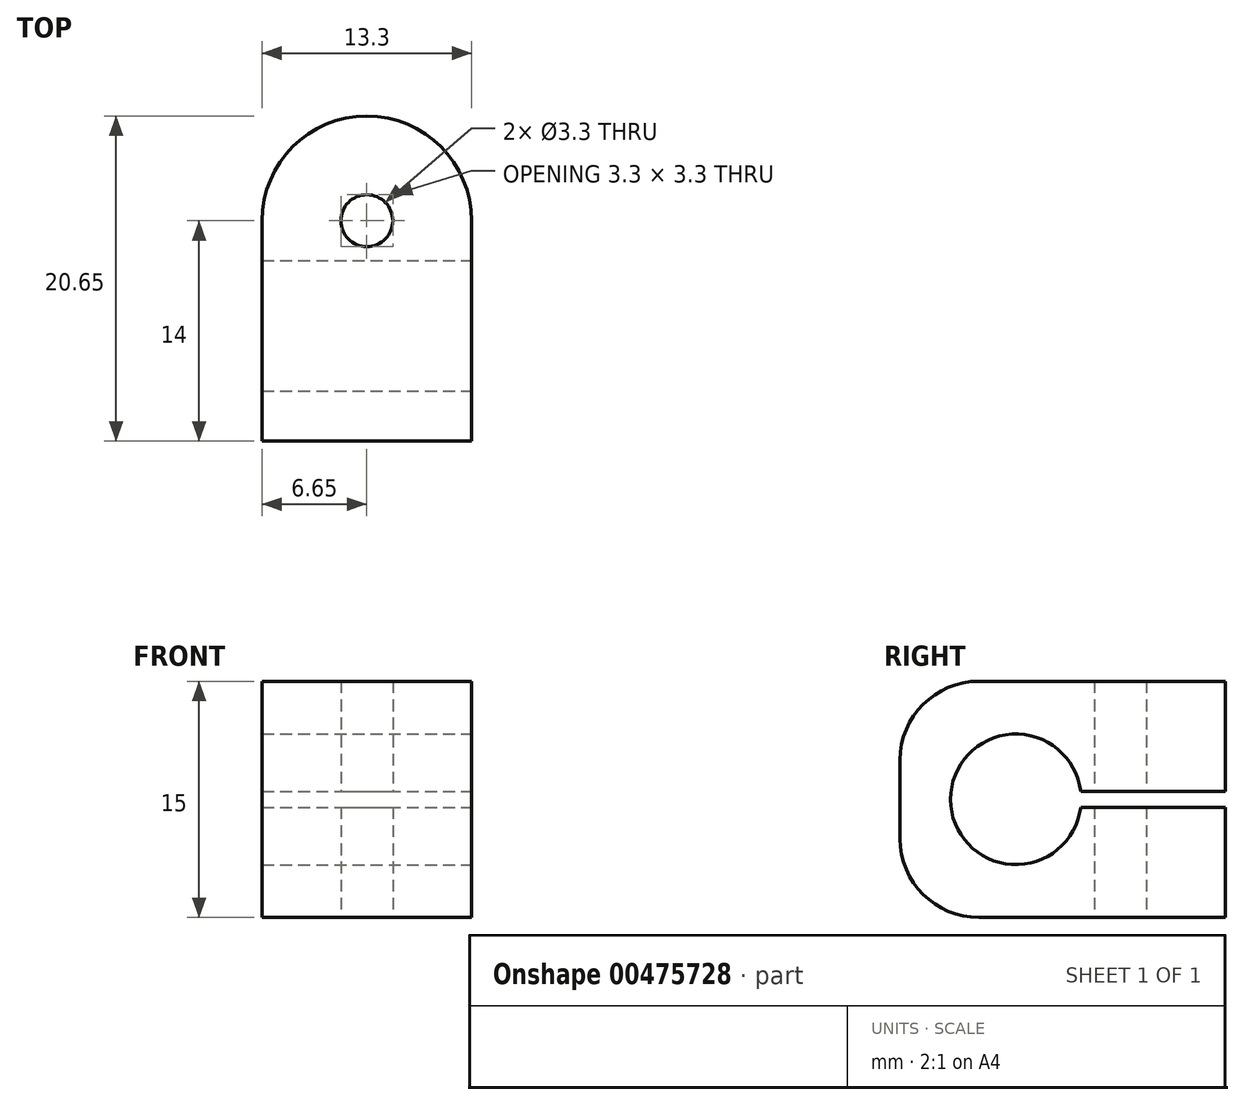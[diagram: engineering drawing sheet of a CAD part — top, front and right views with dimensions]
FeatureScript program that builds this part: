
annotation { "Feature Type Name" : "Feature", "Feature Type Description" : "" }
export const myFeature = defineFeature(function(context is Context, id is Id, definition is map)
    precondition{}
    {
        {
            var Q0;
            Q0=qCreatedBy(makeId("Top.planeOp"),FACE);
            var sketch = newSketch(context, id + "F0", { "sketchPlane" : qUnion([Q0])});
            skCircle(sketch, "E0", {"center": v(0, 0) * mm, "radius": 1.65 * mm});
            skCircle(sketch, "E1", {"center": v(0, 0) * mm, "radius": 6.65 * mm});
            skLineSegment(sketch, "E2.bottom", {"start": v(-6.65, 0) * mm, "end": v(6.65, 0) * mm});
            skLineSegment(sketch, "E2.top", {"start": v(-6.65, -14) * mm, "end": v(6.65, -14) * mm});
            skLineSegment(sketch, "E2.left", {"start": v(-6.65, 0) * mm, "end": v(-6.65, -14) * mm});
            skLineSegment(sketch, "E2.right", {"start": v(6.65, 0) * mm, "end": v(6.65, -14) * mm});
            skSolve(sketch);
        }
        {
            var Q0;
            Q0=qSketchRegion(id+"F0",true);
            extrude(context, id + "F1", {"entities" : qUnion([Q0]), "depth" : 15 * mm});
        }
        {
            var Q0;
            Q0=makeQuery(id+"F1.opExtrude","SWEPT_FACE",FACE,{"disambiguationData":[OSD([sQuery(id+"F0.wireOp",EDGE,"E2.right")])]});
            var sketch = newSketch(context, id + "F2", { "sketchPlane" : qUnion([Q0])});
            skCircle(sketch, "E3", {"center": v(-6.65, 7.5) * mm, "radius": 4.15 * mm});
            skPoint(sketch, "E3.centerSnap0", {"position": v(-14, 7.5) * mm});
            skLineSegment(sketch, "E4.bottom", {"start": v(-2.53, 8) * mm, "end": v(7.86, 8) * mm});
            skLineSegment(sketch, "E4.top", {"start": v(-2.53, 7) * mm, "end": v(7.86, 7) * mm});
            skLineSegment(sketch, "E4.left", {"start": v(-2.53, 8) * mm, "end": v(-2.53, 7) * mm});
            skLineSegment(sketch, "E4.right", {"start": v(7.86, 8) * mm, "end": v(7.86, 7) * mm});
            skLineSegment(sketch, "E5", {"start": v(-1.65, 0) * mm, "end": v(-1.65, 15) * mm});
            skLineSegment(sketch, "E6", {"start": v(1.65, 15) * mm, "end": v(1.65, 0) * mm});
            skLineSegment(sketch, "E7", {"start": v(-14, 7.5) * mm, "end": v(-2.53, 7.5) * mm});
            skSolve(sketch);
        }
        {
            var Q0;
            Q0=qSketchRegion(id+"F2",true);
            extrude(context, id + "F3", {"entities" : qUnion([Q0]), "operationType" : NewBodyOperationType.REMOVE, "endBound" : BoundingType.THROUGH_ALL, "oppositeDirection" : true, "depth" : 25 * mm});
        }
        {
            var Q0;
            Q0=makeQuery(id+"F1.opExtrude","CAP_EDGE",EDGE,{"disambiguationData":[OSD([sQuery(id+"F0.wireOp",EDGE,"E2.top")])],"isStart":false});
            var Q1;
            Q1=makeQuery(id+"F1.opExtrude","CAP_EDGE",EDGE,{"disambiguationData":[OSD([sQuery(id+"F0.wireOp",EDGE,"E2.top")])],"isStart":true});
            fillet(context, id + "F4", {"entities" : qUnion([Q0, Q1]), "radius" : 5 * mm, "tangentPropagation" : true, "allowEdgeOverflow" : false});
        }
    });
